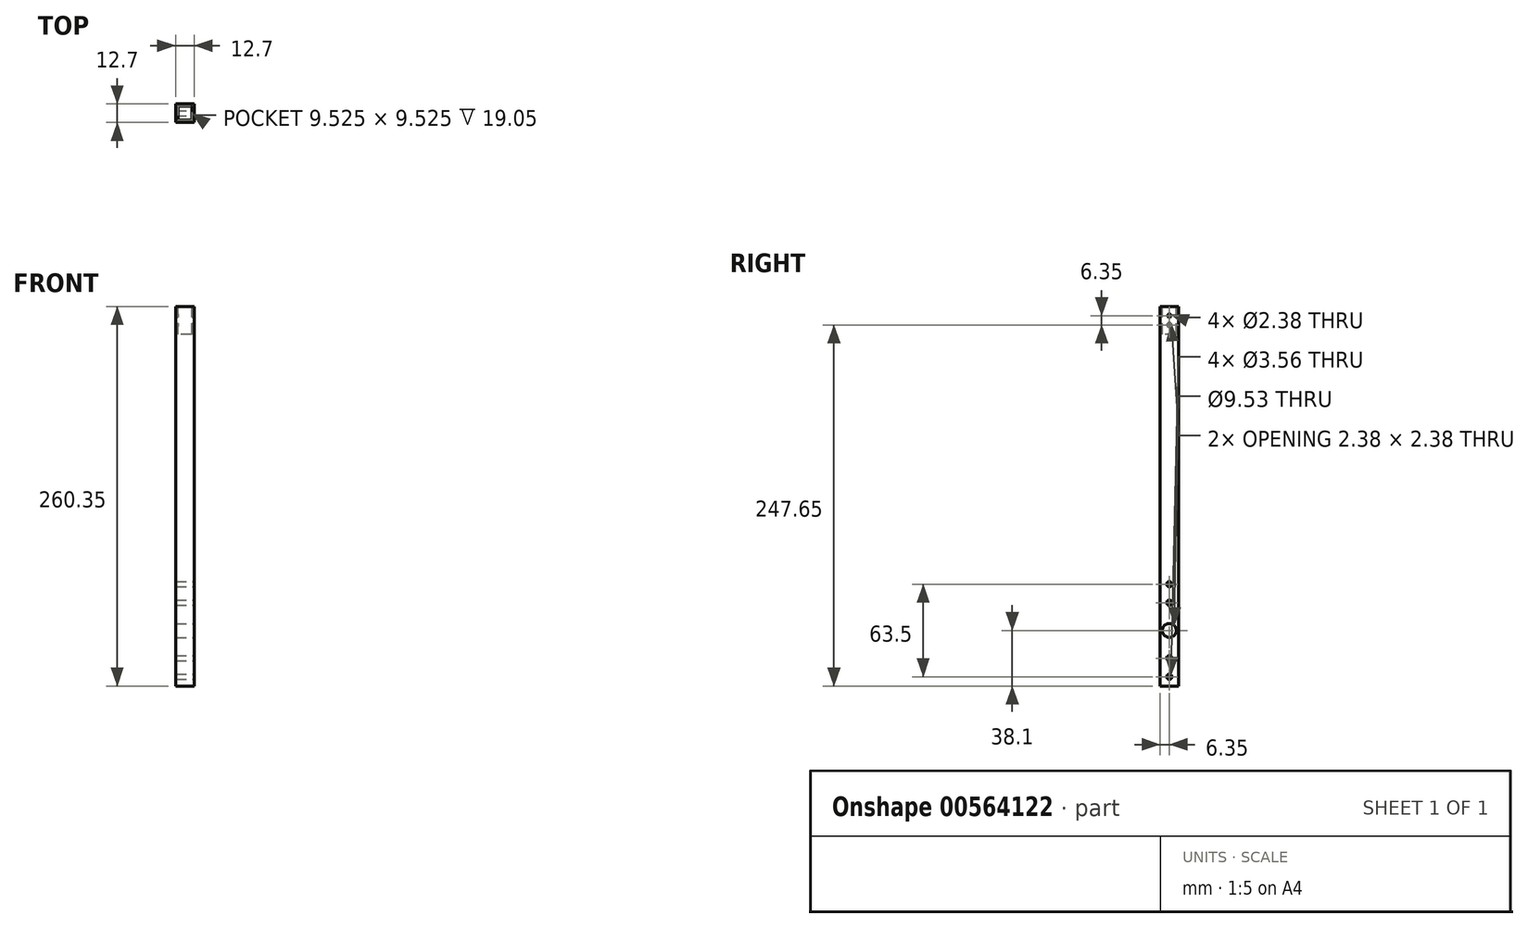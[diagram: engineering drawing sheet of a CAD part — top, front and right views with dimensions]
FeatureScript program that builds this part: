
annotation { "Feature Type Name" : "Feature", "Feature Type Description" : "" }
export const myFeature = defineFeature(function(context is Context, id is Id, definition is map)
    precondition{}
    {
        {
            var Q0;
            Q0=qCreatedBy(makeId("Top.planeOp"),FACE);
            var sketch = newSketch(context, id + "F0", { "sketchPlane" : qUnion([Q0])});
            skLineSegment(sketch, "E0.bottom", {"start": v(-4.76, 4.76) * mm, "end": v(4.76, 4.76) * mm});
            skLineSegment(sketch, "E0.top", {"start": v(-4.76, -4.76) * mm, "end": v(4.76, -4.76) * mm});
            skLineSegment(sketch, "E0.left", {"start": v(-4.76, 4.76) * mm, "end": v(-4.76, -4.76) * mm});
            skLineSegment(sketch, "E0.right", {"start": v(4.76, 4.76) * mm, "end": v(4.76, -4.76) * mm});
            skPoint(sketch, "E0.middle", {"position": v(0, 0) * mm});
            skLineSegment(sketch, "E1.bottom", {"start": v(6.35, 6.35) * mm, "end": v(-6.35, 6.35) * mm});
            skLineSegment(sketch, "E1.top", {"start": v(6.35, -6.35) * mm, "end": v(-6.35, -6.35) * mm});
            skLineSegment(sketch, "E1.left", {"start": v(6.35, 6.35) * mm, "end": v(6.35, -6.35) * mm});
            skLineSegment(sketch, "E1.right", {"start": v(-6.35, 6.35) * mm, "end": v(-6.35, -6.35) * mm});
            skLineSegment(sketch, "E2", {"start": v(0, 4.76) * mm, "end": v(0, 6.35) * mm});
            skLineSegment(sketch, "E3", {"start": v(4.76, 0) * mm, "end": v(6.35, 0) * mm});
            skSolve(sketch);
        }
        {
            var Q0;
            Q0 = qSketchRegion(id + "F0", true);
            var Q1;
            {var subQ1=sQuery(id+"F0.wireOp",EDGE,"E0.top");Q1=makeQuery(id+"F0.imprint","IMPRINT",FACE,{"disambiguationData":[TD([[makeQuery(id+"F0.imprint","IMPRINT",EDGE,{"derivedFrom":subQ1}),1.0]])]});}
            extrude(context, id + "F1", {"entities" : qUnion([Q0, Q1]), "depth" : 260.35 * mm, "offsetDistance" : 25.4 * mm});
        }
        {
            var Q0;
            Q0=makeQuery(id+"F1.opExtrude","SWEPT_FACE",FACE,{"disambiguationData":[OSD([sQuery(id+"F0.wireOp",EDGE,"E1.left")])]});
            var sketch = newSketch(context, id + "F2", { "sketchPlane" : qUnion([Q0])});
            skCircle(sketch, "E4", {"center": v(0, 254) * mm, "radius": 1.2 * mm});
            skCircle(sketch, "E5", {"center": v(0, 247.65) * mm, "radius": 1.2 * mm});
            skSolve(sketch);
        }
        {
            var Q0;
            Q0 = qSketchRegion(id + "F2", true);
            extrude(context, id + "F3", {"entities" : qUnion([Q0]), "operationType" : NewBodyOperationType.REMOVE, "endBound" : BoundingType.THROUGH_ALL, "oppositeDirection" : true, "depth" : 25.4 * mm, "offsetDistance" : 25.4 * mm});
        }
        {
            var Q0;
            Q0=makeQuery(id+"F1.opExtrude","SWEPT_FACE",FACE,{"disambiguationData":[OSD([sQuery(id+"F0.wireOp",EDGE,"E1.left")])]});
            var sketch = newSketch(context, id + "F4", { "sketchPlane" : qUnion([Q0])});
            skLineSegment(sketch, "E6", {"start": v(5.82, 38.1) * mm, "end": v(-5.82, 38.1) * mm});
            skCircle(sketch, "E7", {"center": v(0, 38.1) * mm, "radius": 4.76 * mm});
            skCircle(sketch, "E8", {"center": v(0, 57.15) * mm, "radius": 1.78 * mm});
            skCircle(sketch, "E9", {"center": v(0, 69.85) * mm, "radius": 1.78 * mm});
            skCircle(sketch, "E10.MirrorC", {"center": v(0, 19.05) * mm, "radius": 1.78 * mm});
            skCircle(sketch, "E11.MirrorC", {"center": v(0, 6.35) * mm, "radius": 1.78 * mm});
            skSolve(sketch);
        }
        {
            var Q0;
            Q0 = qSketchRegion(id + "F4", true);
            extrude(context, id + "F5", {"entities" : qUnion([Q0]), "operationType" : NewBodyOperationType.REMOVE, "endBound" : BoundingType.THROUGH_ALL, "oppositeDirection" : true, "depth" : 25.4 * mm, "offsetDistance" : 25.4 * mm});
        }
        {
            var Q0;
            Q0=makeQuery(id+"F1.opExtrude","CAP_FACE",FACE,{"disambiguationData":[OSD([sQuery(id+"F0.wireOp",EDGE,"E1.bottom"),sQuery(id+"F0.wireOp",EDGE,"E1.top"),sQuery(id+"F0.wireOp",EDGE,"E1.left"),sQuery(id+"F0.wireOp",EDGE,"E1.right")])],"isStart":false});
            var sketch = newSketch(context, id + "F6", { "sketchPlane" : qUnion([Q0])});
            skLineSegment(sketch, "E12.bottom", {"start": v(4.76, 4.76) * mm, "end": v(-4.76, 4.76) * mm});
            skLineSegment(sketch, "E12.top", {"start": v(4.76, -4.76) * mm, "end": v(-4.76, -4.76) * mm});
            skLineSegment(sketch, "E12.left", {"start": v(4.76, 4.76) * mm, "end": v(4.76, -4.76) * mm});
            skLineSegment(sketch, "E12.right", {"start": v(-4.76, 4.76) * mm, "end": v(-4.76, -4.76) * mm});
            skPoint(sketch, "E12.middle", {"position": v(0, 0) * mm});
            skSolve(sketch);
        }
        {
            var Q0;
            Q0 = qSketchRegion(id + "F6", true);
            extrude(context, id + "F7", {"entities" : qUnion([Q0]), "operationType" : NewBodyOperationType.REMOVE, "oppositeDirection" : true, "depth" : 19.05 * mm, "offsetDistance" : 25.4 * mm});
        }
    });
